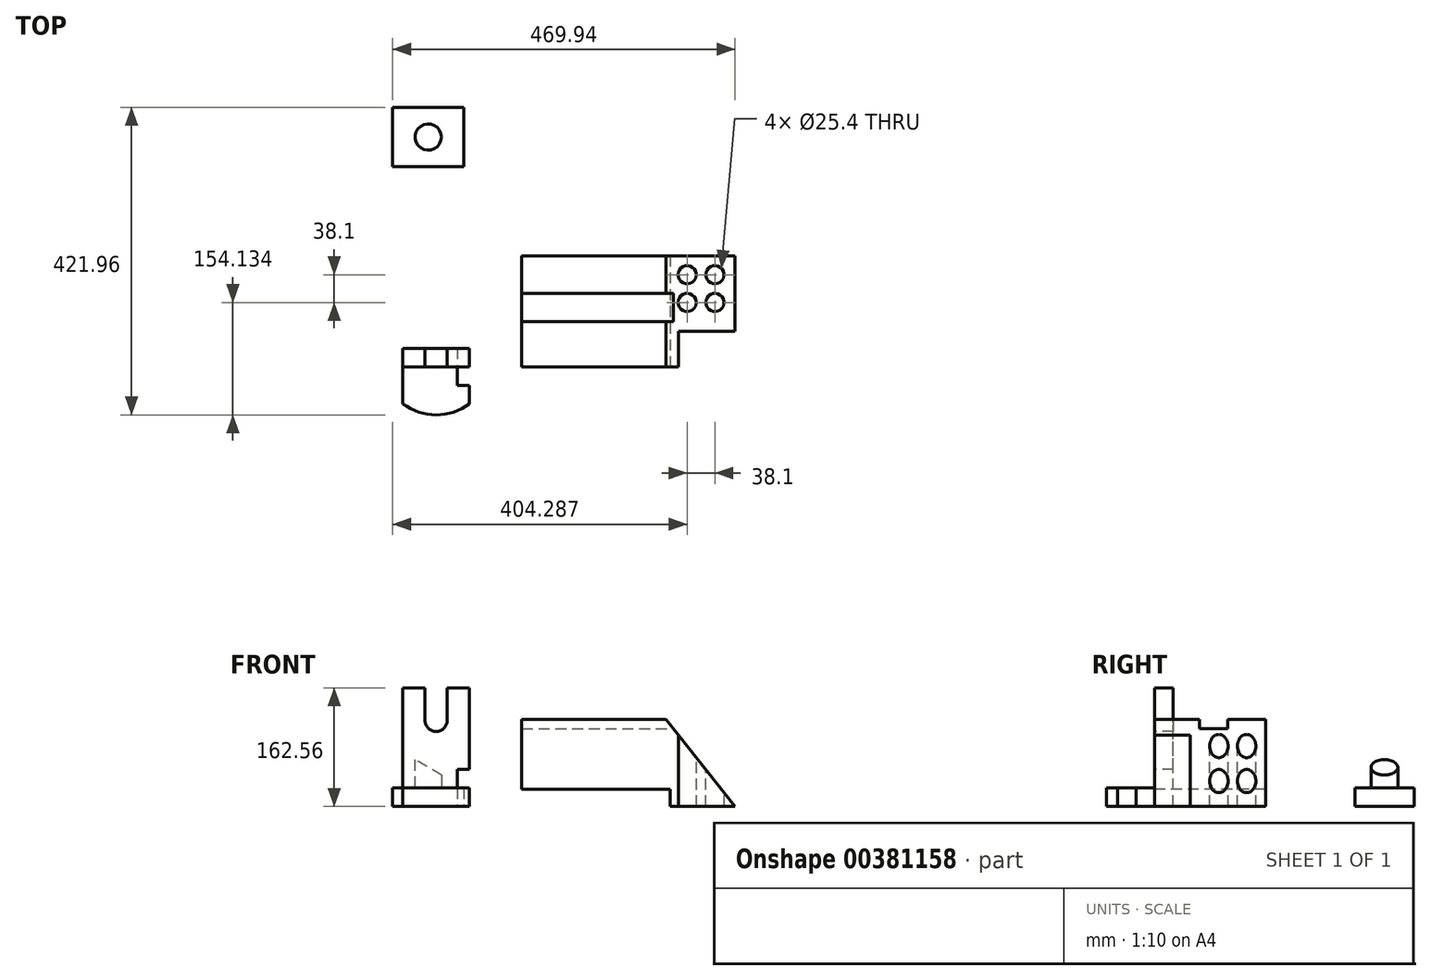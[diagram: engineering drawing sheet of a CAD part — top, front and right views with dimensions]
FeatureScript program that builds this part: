
annotation { "Feature Type Name" : "Feature", "Feature Type Description" : "" }
export const myFeature = defineFeature(function(context is Context, id is Id, definition is map)
    precondition{}
    {
        {
            var Q0;
            Q0=qCreatedBy(makeId("Top.planeOp"),FACE);
            var sketch = newSketch(context, id + "F0", { "sketchPlane" : qUnion([Q0])});
            skLineSegment(sketch, "E0.bottom", {"start": v(-215.42, 32.83) * mm, "end": v(-117.67, 32.83) * mm});
            skLineSegment(sketch, "E0.top", {"start": v(-215.42, -48.33) * mm, "end": v(-117.67, -48.33) * mm});
            skLineSegment(sketch, "E0.left", {"start": v(-215.42, 32.83) * mm, "end": v(-215.42, -48.33) * mm});
            skLineSegment(sketch, "E0.right", {"start": v(-117.67, 32.83) * mm, "end": v(-117.67, -48.33) * mm});
            skLineSegment(sketch, "E1", {"start": v(-166.54, 32.83) * mm, "end": v(-166.54, -48.33) * mm, "construction": true});
            skCircle(sketch, "E2", {"center": v(-166.54, -7.75) * mm, "radius": 18.37 * mm});
            skSolve(sketch);
        }
        {
            var Q0;
            Q0 = qSketchRegion(id + "F0", true);
            var Q1;
            Q1=makeQuery(id+"F0.imprint","IMPRINT",FACE,{"disambiguationData":[TD([[makeQuery(id+"F0.imprint","IMPRINT",EDGE,{"derivedFrom":sQuery(id+"F0.wireOp",EDGE,"E2")}),1.0]])]});
            extrude(context, id + "F1", {"entities" : qUnion([Q0, Q1]), "depth" : 25.4 * mm});
        }
        {
            var Q0;
            Q0=makeQuery(id+"F1.opExtrude","CAP_EDGE",EDGE,{"disambiguationData":[OSD([sQuery(id+"F0.wireOp",EDGE,"E0.right")])],"isStart":false});
            var Q1;
            Q1=makeQuery(id+"F1.opExtrude","CAP_FACE",FACE,{"disambiguationData":[OSD([sQuery(id+"F0.wireOp",EDGE,"E0.bottom"),sQuery(id+"F0.wireOp",EDGE,"E0.top"),sQuery(id+"F0.wireOp",EDGE,"E0.left"),sQuery(id+"F0.wireOp",EDGE,"E0.right")])],"isStart":false});
            cPlane(context, id + "F2", {"entities" : qUnion([Q0, Q1]), "cplaneType" : CPlaneType.LINE_ANGLE, "offset" : 25.4 * mm, "angle" : 30 * degree, "oppositeDirection" : true, "width" : 152.4 * mm, "height" : 152.4 * mm});
        }
        {
            var Q0;
            Q0=makeQuery(id+"F0.imprint","IMPRINT",FACE,{"disambiguationData":[TD([[makeQuery(id+"F0.imprint","IMPRINT",EDGE,{"derivedFrom":sQuery(id+"F0.wireOp",EDGE,"E2")}),1.0]])]});
            var Q1;
            Q1=qCreatedBy(id+"F2.planeOp",FACE);
            extrude(context, id + "F3", {"entities" : qUnion([Q0]), "operationType" : NewBodyOperationType.ADD, "endBound" : BoundingType.UP_TO_SURFACE, "endBoundEntityFace" : qUnion([Q1]), "depth" : 25.4 * mm});
        }
        {
            var Q0;
            Q0=qCreatedBy(makeId("Front.planeOp"),FACE);
            var sketch = newSketch(context, id + "F4", { "sketchPlane" : qUnion([Q0])});
            skLineSegment(sketch, "E3", {"start": v(50.37, 0) * mm, "end": v(183.27, 0) * mm});
            skLineSegment(sketch, "E4", {"start": v(183.27, 0) * mm, "end": v(183.27, 23.83) * mm});
            skLineSegment(sketch, "E5", {"start": v(183.27, 23.83) * mm, "end": v(118.93, 93.24) * mm});
            skLineSegment(sketch, "E6", {"start": v(118.93, 93.24) * mm, "end": v(50.37, 93.24) * mm});
            skLineSegment(sketch, "E7", {"start": v(50.37, 93.24) * mm, "end": v(50.37, 0) * mm});
            skLineSegment(sketch, "E8.0", {"start": v(124.48, 105.94) * mm, "end": v(50.37, 105.94) * mm});
            skLineSegment(sketch, "E8.1", {"start": v(183.27, 42.5) * mm, "end": v(124.48, 105.94) * mm});
            skLineSegment(sketch, "E9", {"start": v(50.37, 93.24) * mm, "end": v(50.37, 105.94) * mm});
            skLineSegment(sketch, "E10", {"start": v(183.27, 23.83) * mm, "end": v(183.27, 42.5) * mm});
            skSolve(sketch);
        }
        {
            var Q0;
            Q0=makeQuery(id+"F4.imprint","IMPRINT",FACE,{"disambiguationData":[TD([[makeQuery(id+"F4.imprint","IMPRINT",EDGE,{"derivedFrom":sQuery(id+"F4.wireOp",EDGE,"E3")}),1.0]])]});
            extrude(context, id + "F5", {"entities" : qUnion([Q0]), "depth" : 101.6 * mm});
        }
        {
            var Q0;
            Q0=makeQuery(id+"F4.imprint","IMPRINT",FACE,{"disambiguationData":[TD([[makeQuery(id+"F4.imprint","IMPRINT",EDGE,{"derivedFrom":sQuery(id+"F4.wireOp",EDGE,"E5")}),-1.0]])]});
            extrude(context, id + "F6", {"entities" : qUnion([Q0]), "operationType" : NewBodyOperationType.ADD, "depth" : 19.05 * mm});
        }
        {
            var Q0;
            Q0=makeQuery(id+"F6.boolean.opBoolean","MERGE",FACE,{"derivedFrom":[makeQuery(id+"F5.opExtrude","SWEPT_FACE",FACE,{"disambiguationData":[OSD([sQuery(id+"F4.wireOp",EDGE,"E7")])]}),makeQuery(id+"F6.opExtrude","SWEPT_FACE",FACE,{"disambiguationData":[OSD([sQuery(id+"F4.wireOp",EDGE,"E9")])]})]});
            var sketch = newSketch(context, id + "F7", { "sketchPlane" : qUnion([Q0])});
            skCircle(sketch, "E11", {"center": v(51.66, 50.19) * mm, "radius": 16.9 * mm});
            skLineSegment(sketch, "E12.0", {"start": v(101.6, 0) * mm, "end": v(0, 0) * mm});
            skLineSegment(sketch, "E13.0", {"start": v(101.6, 93.24) * mm, "end": v(101.6, 0) * mm});
            skSolve(sketch);
        }
        {
            var Q0;
            Q0 = qSketchRegion(id + "F7", true);
            extrude(context, id + "F8", {"entities" : qUnion([Q0]), "operationType" : NewBodyOperationType.ADD, "endBound" : BoundingType.UP_TO_NEXT, "oppositeDirection" : true, "depth" : 25.4 * mm});
        }
        {
            var Q0;
            Q0=makeQuery(id+"F7.imprint","IMPRINT",FACE,{"disambiguationData":[TD([[makeQuery(id+"F7.imprint","IMPRINT",EDGE,{"derivedFrom":sQuery(id+"F7.wireOp",EDGE,"E11")}),-1.0]])]});
            var Q1;
            Q1=sQuery(id+"F7.wireOp",EDGE,"E11");
            extrude(context, id + "F9", {"entities" : qUnion([Q0]), "operationType" : NewBodyOperationType.REMOVE, "surfaceEntities" : qUnion([Q1]), "endBound" : BoundingType.UP_TO_NEXT, "oppositeDirection" : true, "depth" : 25.4 * mm});
        }
        {
            var Q0;
            Q0=makeQuery(id+"F7.imprint","IMPRINT",FACE,{"disambiguationData":[TD([[makeQuery(id+"F7.imprint","IMPRINT",EDGE,{"derivedFrom":sQuery(id+"F7.wireOp",EDGE,"E11")}),1.0]])]});
            var Q1;
            Q1=sQuery(id+"F7.wireOp",EDGE,"E11");
            extrude(context, id + "F10", {"entities" : qUnion([Q0]), "operationType" : NewBodyOperationType.REMOVE, "surfaceEntities" : qUnion([Q1]), "endBound" : BoundingType.UP_TO_NEXT, "oppositeDirection" : true, "depth" : 25.4 * mm});
        }
        {
            var Q0;
            Q0=qCreatedBy(makeId("Front.planeOp"),FACE);
            cPlane(context, id + "F11", {"entities" : qUnion([Q0]), "cplaneType" : CPlaneType.OFFSET, "offset" : 323.09 * mm, "width" : 152.4 * mm, "height" : 152.4 * mm});
        }
        {
            var Q0;
            Q0=qCreatedBy(id+"F11.planeOp",FACE);
            var sketch = newSketch(context, id + "F12", { "sketchPlane" : qUnion([Q0])});
            skArc(sketch, "E14", {"start": v(-170.85, 118.1) * mm, "mid": v(-155.6, 102.87) * mm, "end": v(-140.37, 118.11) * mm});
            skLineSegment(sketch, "E15", {"start": v(-126.4, 0) * mm, "end": v(-126.4, 50.8) * mm});
            skLineSegment(sketch, "E16", {"start": v(-126.4, 50.8) * mm, "end": v(-109.89, 50.8) * mm});
            skLineSegment(sketch, "E17", {"start": v(-109.89, 50.8) * mm, "end": v(-109.89, 162.56) * mm});
            skLineSegment(sketch, "E18", {"start": v(-109.89, 162.56) * mm, "end": v(-140.37, 162.56) * mm});
            skLineSegment(sketch, "E19", {"start": v(-140.37, 162.56) * mm, "end": v(-140.37, 118.11) * mm});
            skLineSegment(sketch, "E20", {"start": v(-126.4, 0) * mm, "end": v(-201.33, 0) * mm});
            skLineSegment(sketch, "E21", {"start": v(-201.33, 0) * mm, "end": v(-201.33, 162.56) * mm});
            skLineSegment(sketch, "E22", {"start": v(-201.33, 162.56) * mm, "end": v(-170.85, 162.56) * mm});
            skLineSegment(sketch, "E23", {"start": v(-170.85, 162.56) * mm, "end": v(-170.85, 118.1) * mm});
            skSolve(sketch);
        }
        {
            var Q0;
            Q0=makeQuery(id+"F12.imprint","IMPRINT",FACE,{"disambiguationData":[TD([[makeQuery(id+"F12.imprint","IMPRINT",EDGE,{"derivedFrom":sQuery(id+"F12.wireOp",EDGE,"E14")}),-1.0]])]});
            extrude(context, id + "F13", {"entities" : qUnion([Q0]), "oppositeDirection" : true, "depth" : 25.4 * mm});
        }
        {
            var Q0;
            Q0=qCreatedBy(makeId("Top.planeOp"),FACE);
            var sketch = newSketch(context, id + "F14", { "sketchPlane" : qUnion([Q0])});
            skLineSegment(sketch, "E24.0", {"start": v(-126.4, -323.09) * mm, "end": v(-201.33, -323.09) * mm});
            skLineSegment(sketch, "E25", {"start": v(-201.33, -323.09) * mm, "end": v(-201.33, -373.89) * mm});
            skLineSegment(sketch, "E26", {"start": v(-126.4, -323.09) * mm, "end": v(-126.4, -348.49) * mm});
            skLineSegment(sketch, "E27", {"start": v(-109.89, -348.49) * mm, "end": v(-109.89, -373.89) * mm});
            skLineSegment(sketch, "E28", {"start": v(-126.4, -348.49) * mm, "end": v(-109.89, -348.49) * mm});
            skArc(sketch, "E29.converted", {"start": v(-201.33, -373.89) * mm, "mid": v(-155.6, -389.13) * mm, "end": v(-109.89, -373.89) * mm});
            skSolve(sketch);
        }
        {
            var Q0;
            Q0=makeQuery(id+"F14.imprint","IMPRINT",FACE,{"disambiguationData":[TD([[makeQuery(id+"F14.imprint","IMPRINT",EDGE,{"derivedFrom":sQuery(id+"F14.wireOp",EDGE,"E24.0")}),1.0]])]});
            extrude(context, id + "F15", {"entities" : qUnion([Q0]), "operationType" : NewBodyOperationType.ADD, "depth" : 25.4 * mm});
        }
        {
            var Q0;
            Q0=qCreatedBy(id+"F11.planeOp",FACE);
            var sketch = newSketch(context, id + "F16", { "sketchPlane" : qUnion([Q0])});
            skLineSegment(sketch, "E30", {"start": v(-38.07, 0) * mm, "end": v(254.52, 0) * mm});
            skLineSegment(sketch, "E31", {"start": v(254.52, 0) * mm, "end": v(160.05, 119.15) * mm});
            skLineSegment(sketch, "E32", {"start": v(160.05, 119.15) * mm, "end": v(-38.07, 119.15) * mm});
            skLineSegment(sketch, "E33", {"start": v(-38.07, 119.15) * mm, "end": v(-38.07, 0) * mm});
            skSolve(sketch);
        }
        {
            var Q0;
            Q0=makeQuery(id+"F16.imprint","IMPRINT",FACE,{"disambiguationData":[TD([[makeQuery(id+"F16.imprint","IMPRINT",EDGE,{"derivedFrom":sQuery(id+"F16.wireOp",EDGE,"E30")}),1.0]])]});
            extrude(context, id + "F17", {"entities" : qUnion([Q0]), "oppositeDirection" : true, "depth" : 152.4 * mm});
        }
        {
            var Q0;
            Q0=makeQuery(id+"F17.opExtrude","SWEPT_FACE",FACE,{"disambiguationData":[OSD([sQuery(id+"F16.wireOp",EDGE,"E32")])]});
            var sketch = newSketch(context, id + "F18", { "sketchPlane" : qUnion([Q0])});
            skCircle(sketch, "E34", {"center": v(188.87, -196.9) * mm, "radius": 12.7 * mm});
            skCircle(sketch, "E35", {"center": v(226.97, -196.9) * mm, "radius": 12.7 * mm});
            skCircle(sketch, "E36", {"center": v(188.87, -235) * mm, "radius": 12.7 * mm});
            skCircle(sketch, "E37", {"center": v(226.97, -235) * mm, "radius": 12.7 * mm});
            skLineSegment(sketch, "E38.bottom", {"start": v(258.03, -325) * mm, "end": v(176.75, -325) * mm});
            skLineSegment(sketch, "E38.top", {"start": v(258.03, -274.2) * mm, "end": v(176.75, -274.2) * mm});
            skLineSegment(sketch, "E38.left", {"start": v(258.03, -325) * mm, "end": v(258.03, -274.2) * mm});
            skLineSegment(sketch, "E38.right", {"start": v(176.75, -325) * mm, "end": v(176.75, -274.2) * mm});
            skSolve(sketch);
        }
        {
            var Q0;
            Q0=makeQuery(id+"F18.imprint","IMPRINT",FACE,{"disambiguationData":[TD([[makeQuery(id+"F18.imprint","IMPRINT",EDGE,{"derivedFrom":sQuery(id+"F18.wireOp",EDGE,"E38.bottom")}),-1.0]])]});
            extrude(context, id + "F19", {"entities" : qUnion([Q0]), "operationType" : NewBodyOperationType.REMOVE, "oppositeDirection" : true, "depth" : 168.15 * mm});
        }
        {
            var Q0;
            Q0=makeQuery(id+"F18.imprint","IMPRINT",FACE,{"disambiguationData":[TD([[makeQuery(id+"F18.imprint","IMPRINT",EDGE,{"derivedFrom":sQuery(id+"F18.wireOp",EDGE,"E35")}),1.0]])]});
            var Q1;
            Q1=makeQuery(id+"F18.imprint","IMPRINT",FACE,{"disambiguationData":[TD([[makeQuery(id+"F18.imprint","IMPRINT",EDGE,{"derivedFrom":sQuery(id+"F18.wireOp",EDGE,"E37")}),1.0]])]});
            var Q2;
            Q2=makeQuery(id+"F18.imprint","IMPRINT",FACE,{"disambiguationData":[TD([[makeQuery(id+"F18.imprint","IMPRINT",EDGE,{"derivedFrom":sQuery(id+"F18.wireOp",EDGE,"E36")}),1.0]])]});
            var Q3;
            Q3=makeQuery(id+"F18.imprint","IMPRINT",FACE,{"disambiguationData":[TD([[makeQuery(id+"F18.imprint","IMPRINT",EDGE,{"derivedFrom":sQuery(id+"F18.wireOp",EDGE,"E34")}),1.0]])]});
            var Q4;
            Q4=sQuery(id+"F18.wireOp",EDGE,"E35");
            var Q5;
            Q5=sQuery(id+"F18.wireOp",EDGE,"E37");
            var Q6;
            Q6=sQuery(id+"F18.wireOp",EDGE,"E36");
            var Q7;
            Q7=sQuery(id+"F18.wireOp",EDGE,"E34");
            extrude(context, id + "F20", {"entities" : qUnion([Q0, Q1, Q2, Q3]), "operationType" : NewBodyOperationType.REMOVE, "surfaceEntities" : qUnion([Q4, Q5, Q6, Q7]), "oppositeDirection" : true, "depth" : 179.32 * mm});
        }
        {
            var Q0;
            {var subQ0=sQuery(id+"F16.wireOp",EDGE,"E32");Q0=makeQuery(id+"F18.imprint","IMPRINT",FACE,{"disambiguationData":[TD([[makeQuery(id+"F18.imprint","IMPRINT",EDGE,{"derivedFrom":makeQuery(id+"F17.opExtrude","CAP_EDGE",EDGE,{"disambiguationData":[OSD([subQ0])],"isStart":true})}),-1.0]])]});}
            var sketch = newSketch(context, id + "F21", { "sketchPlane" : qUnion([Q0])});
            skLineSegment(sketch, "E39.bottom", {"start": v(-49.15, -222.68) * mm, "end": v(306.63, -222.68) * mm});
            skLineSegment(sketch, "E39.top", {"start": v(-49.15, -261.3) * mm, "end": v(306.63, -261.3) * mm});
            skLineSegment(sketch, "E39.left", {"start": v(-49.15, -222.68) * mm, "end": v(-49.15, -261.3) * mm});
            skLineSegment(sketch, "E39.right", {"start": v(306.63, -222.68) * mm, "end": v(306.63, -261.3) * mm});
            skSolve(sketch);
        }
        {
            var Q0;
            Q0 = qSketchRegion(id + "F21", true);
            extrude(context, id + "F22", {"entities" : qUnion([Q0]), "operationType" : NewBodyOperationType.REMOVE, "oppositeDirection" : true, "depth" : 12.7 * mm});
        }
        {
            var Q0;
            Q0=makeQuery(id+"F17.opExtrude","CAP_FACE",FACE,{"disambiguationData":[OSD([sQuery(id+"F16.wireOp",EDGE,"E30"),sQuery(id+"F16.wireOp",EDGE,"E31"),sQuery(id+"F16.wireOp",EDGE,"E32"),sQuery(id+"F16.wireOp",EDGE,"E33")])],"isStart":true});
            var sketch = newSketch(context, id + "F23", { "sketchPlane" : qUnion([Q0])});
            skLineSegment(sketch, "E40.bottom", {"start": v(-88.39, -9.68) * mm, "end": v(165.52, -9.68) * mm});
            skLineSegment(sketch, "E40.top", {"start": v(-88.39, 23.4) * mm, "end": v(165.52, 23.4) * mm});
            skLineSegment(sketch, "E40.left", {"start": v(-88.39, -9.68) * mm, "end": v(-88.39, 23.4) * mm});
            skLineSegment(sketch, "E40.right", {"start": v(165.52, -9.68) * mm, "end": v(165.52, 23.4) * mm});
            skSolve(sketch);
        }
        {
            var Q0;
            Q0 = qSketchRegion(id + "F23", true);
            extrude(context, id + "F24", {"entities" : qUnion([Q0]), "operationType" : NewBodyOperationType.REMOVE, "oppositeDirection" : true, "depth" : 304.8 * mm});
        }
    });
